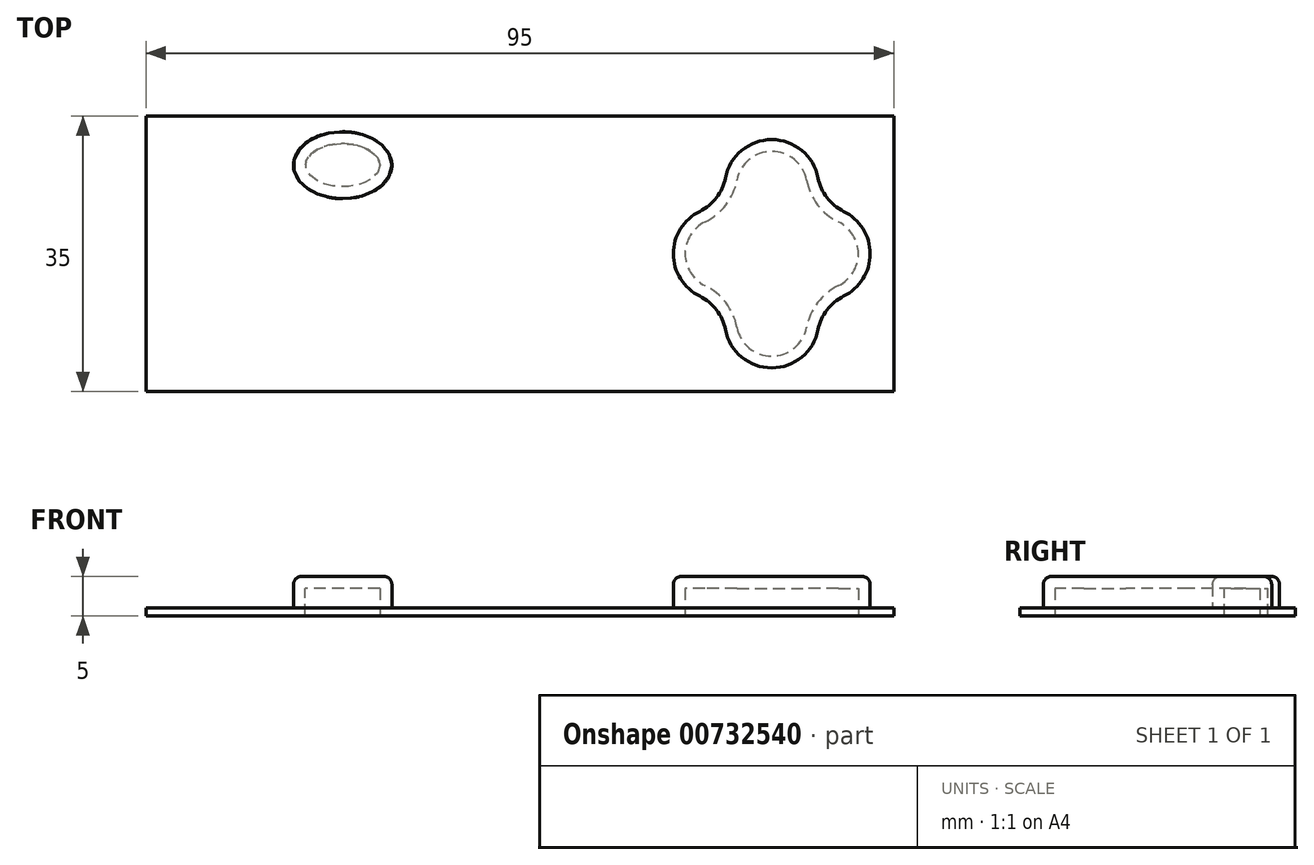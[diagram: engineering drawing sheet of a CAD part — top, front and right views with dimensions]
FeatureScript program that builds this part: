
annotation { "Feature Type Name" : "Feature", "Feature Type Description" : "" }
export const myFeature = defineFeature(function(context is Context, id is Id, definition is map)
    precondition{}
    {
        {
            var Q0;
            Q0=qCreatedBy(makeId("Top.planeOp"),FACE);
            var sketch = newSketch(context, id + "F0", { "sketchPlane" : qUnion([Q0])});
            skLineSegment(sketch, "E0.bottom", {"start": v(47.5, 17.5) * mm, "end": v(-47.5, 17.5) * mm});
            skLineSegment(sketch, "E0.top", {"start": v(47.5, -17.5) * mm, "end": v(-47.5, -17.5) * mm});
            skLineSegment(sketch, "E0.left", {"start": v(47.5, 17.5) * mm, "end": v(47.5, -17.5) * mm});
            skLineSegment(sketch, "E0.right", {"start": v(-47.5, 17.5) * mm, "end": v(-47.5, -17.5) * mm});
            skPoint(sketch, "E0.middle", {"position": v(0, 0) * mm});
            skSolve(sketch);
        }
        {
            var Q0;
            Q0 = qSketchRegion(id + "F0", true);
            extrude(context, id + "F1", {"entities" : qUnion([Q0]), "depth" : 1 * mm, "offsetDistance" : 25 * mm});
        }
        {
            var Q0;
            Q0=makeQuery(id+"F1.opExtrude","CAP_FACE",FACE,{"disambiguationData":[OSD([sQuery(id+"F0.wireOp",EDGE,"E0.bottom"),sQuery(id+"F0.wireOp",EDGE,"E0.top"),sQuery(id+"F0.wireOp",EDGE,"E0.left"),sQuery(id+"F0.wireOp",EDGE,"E0.right")])],"isStart":false});
            var sketch = newSketch(context, id + "F2", { "sketchPlane" : qUnion([Q0])});
            skEllipse(sketch, "E1", {"center": v(-22.5, 11.25) * mm, "majorRadius": 6.25 * mm, "minorRadius": 4.25 * mm, "majorAxis": v(1, 0)});
            skArc(sketch, "E2", {"start": v(37.4, 5.9) * mm, "mid": v(32, 14.5) * mm, "end": v(26.6, 5.9) * mm});
            skArc(sketch, "E3", {"start": v(26.6, 5.9) * mm, "mid": v(19.5, 0) * mm, "end": v(26.6, -5.9) * mm});
            skArc(sketch, "E4", {"start": v(37.4, -5.9) * mm, "mid": v(44.5, 0) * mm, "end": v(37.4, 5.9) * mm});
            skArc(sketch, "E5", {"start": v(26.6, -5.9) * mm, "mid": v(32, -14.5) * mm, "end": v(37.4, -5.9) * mm});
            skSolve(sketch);
        }
        {
            var Q0;
            Q0 = qSketchRegion(id + "F2", true);
            extrude(context, id + "F3", {"entities" : qUnion([Q0]), "operationType" : NewBodyOperationType.ADD, "depth" : 4 * mm, "offsetDistance" : 25 * mm});
        }
        {
            var Q0;
            Q0=makeQuery(id+"F3.opExtrude","SWEPT_EDGE",EDGE,{"disambiguationData":[OSD([sQuery(id+"F2.wireOp",EDGE,"E3"),sQuery(id+"F2.wireOp",EDGE,"E5")])]});
            var Q1;
            Q1=makeQuery(id+"F3.opExtrude","SWEPT_EDGE",EDGE,{"disambiguationData":[OSD([sQuery(id+"F2.wireOp",EDGE,"E4"),sQuery(id+"F2.wireOp",EDGE,"E5")])]});
            var Q2;
            Q2=makeQuery(id+"F3.opExtrude","SWEPT_EDGE",EDGE,{"disambiguationData":[OSD([sQuery(id+"F2.wireOp",EDGE,"E2"),sQuery(id+"F2.wireOp",EDGE,"E4")])]});
            var Q3;
            Q3=makeQuery(id+"F3.opExtrude","SWEPT_EDGE",EDGE,{"disambiguationData":[OSD([sQuery(id+"F2.wireOp",EDGE,"E2"),sQuery(id+"F2.wireOp",EDGE,"E3")])]});
            fillet(context, id + "F4", {"entities" : qUnion([Q0, Q1, Q2, Q3]), "radius" : 6 * mm, "tangentPropagation" : true, "allowEdgeOverflow" : false});
        }
        {
            var Q0;
            Q0=makeQuery(id+"F3.opExtrude","CAP_FACE",FACE,{"disambiguationData":[OSD([sQuery(id+"F2.wireOp",EDGE,"E2"),sQuery(id+"F2.wireOp",EDGE,"E3"),sQuery(id+"F2.wireOp",EDGE,"E4"),sQuery(id+"F2.wireOp",EDGE,"E5")])],"isStart":false});
            var Q1;
            Q1=makeQuery(id+"F3.opExtrude","CAP_FACE",FACE,{"disambiguationData":[OSD([sQuery(id+"F2.wireOp",EDGE,"E1")])],"isStart":false});
            fillet(context, id + "F5", {"entities" : qUnion([Q0, Q1]), "radius" : 1 * mm, "tangentPropagation" : true, "allowEdgeOverflow" : false});
        }
        {
            var Q0;
            Q0=makeQuery(id+"F1.opExtrude","CAP_FACE",FACE,{"disambiguationData":[OSD([sQuery(id+"F0.wireOp",EDGE,"E0.bottom"),sQuery(id+"F0.wireOp",EDGE,"E0.top"),sQuery(id+"F0.wireOp",EDGE,"E0.left"),sQuery(id+"F0.wireOp",EDGE,"E0.right")])],"isStart":true});
            shell(context, id + "F6", {"entities" : qUnion([Q0]), "thickness" : 1.5 * mm});
        }
    });
